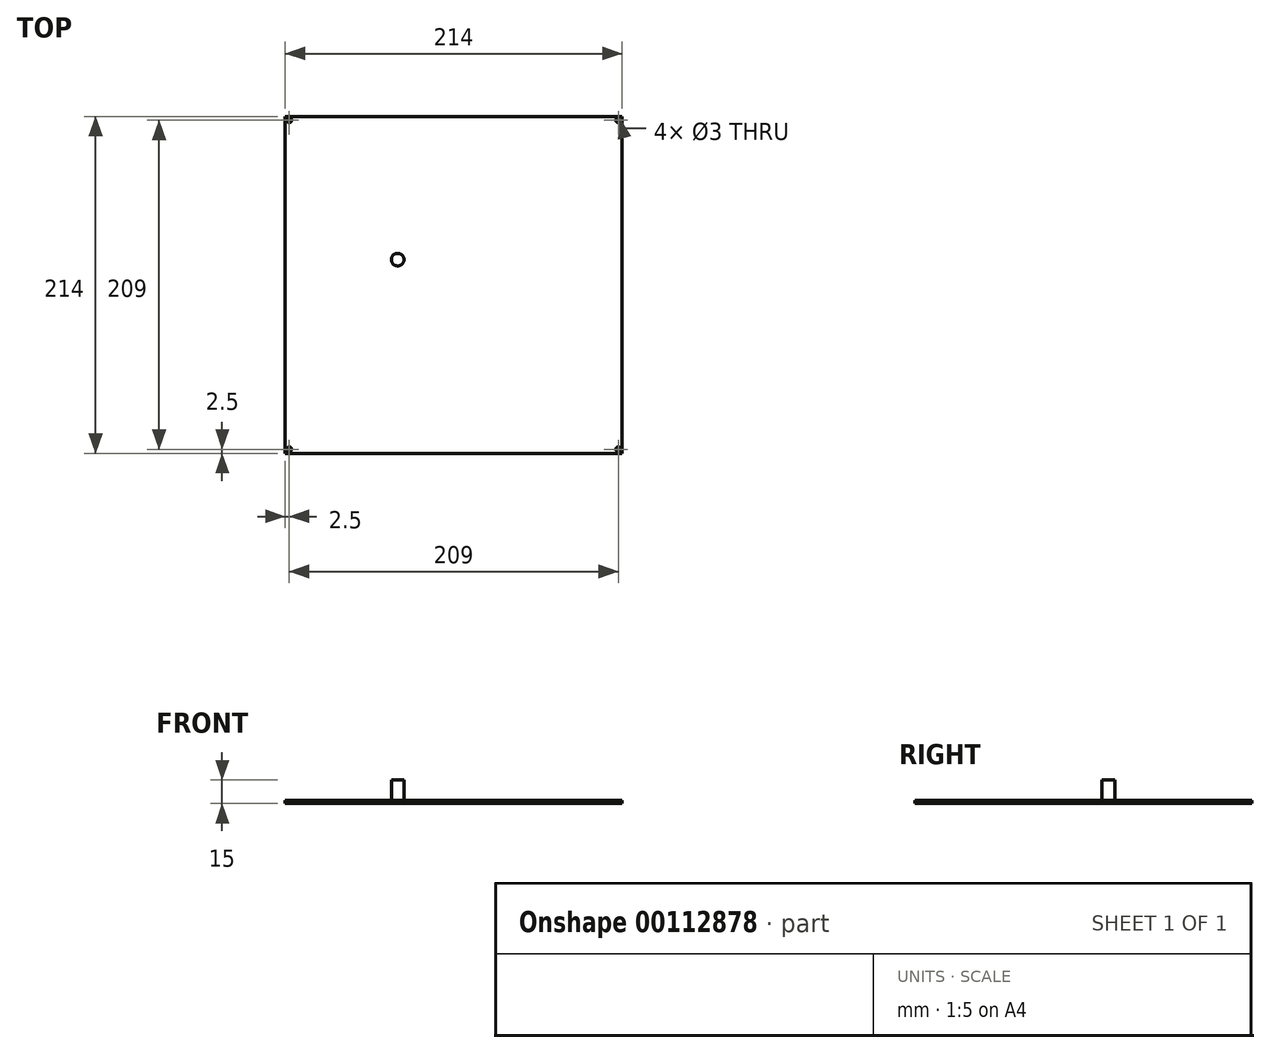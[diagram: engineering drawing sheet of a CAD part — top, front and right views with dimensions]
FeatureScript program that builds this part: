
annotation { "Feature Type Name" : "Feature", "Feature Type Description" : "" }
export const myFeature = defineFeature(function(context is Context, id is Id, definition is map)
    precondition{}
    {
        {
            var Q0;
            Q0=qCreatedBy(makeId("Top.planeOp"),FACE);
            var sketch = newSketch(context, id + "F0", { "sketchPlane" : qUnion([Q0])});
            skLineSegment(sketch, "E0.bottom", {"start": v(107, 107) * mm, "end": v(-107, 107) * mm});
            skLineSegment(sketch, "E0.top", {"start": v(107, -107) * mm, "end": v(-107, -107) * mm});
            skLineSegment(sketch, "E0.left", {"start": v(107, 107) * mm, "end": v(107, -107) * mm});
            skLineSegment(sketch, "E0.right", {"start": v(-107, 107) * mm, "end": v(-107, -107) * mm});
            skPoint(sketch, "E0.middle", {"position": v(0, 0) * mm});
            skLineSegment(sketch, "E1.bottom", {"start": v(104.5, 104.5) * mm, "end": v(-104.5, 104.5) * mm, "construction": true});
            skLineSegment(sketch, "E1.top", {"start": v(104.5, -104.5) * mm, "end": v(-104.5, -104.5) * mm, "construction": true});
            skLineSegment(sketch, "E1.left", {"start": v(104.5, 104.5) * mm, "end": v(104.5, -104.5) * mm, "construction": true});
            skLineSegment(sketch, "E1.right", {"start": v(-104.5, 104.5) * mm, "end": v(-104.5, -104.5) * mm, "construction": true});
            skSolve(sketch);
        }
        {
            var Q0;
            Q0=makeQuery(id+"F0.imprint","IMPRINT",FACE,{"disambiguationData":[TD([[makeQuery(id+"F0.imprint","IMPRINT",EDGE,{"derivedFrom":sQuery(id+"F0.wireOp",EDGE,"E0.bottom")}),1.0]])]});
            extrude(context, id + "F1", {"entities" : qUnion([Q0]), "depth" : 2 * mm});
        }
        {
            var Q0;
            Q0=sQuery(id+"F0.wireOp",VERTEX,"E1.right.start");
            var Q1;
            Q1=sQuery(id+"F0.wireOp",VERTEX,"E1.left.start");
            var Q2;
            Q2=sQuery(id+"F0.wireOp",VERTEX,"E1.right.end");
            var Q3;
            Q3=sQuery(id+"F0.wireOp",VERTEX,"E1.left.end");
            var Q4;
            Q4=makeQuery(id+"F1.opExtrude","SWEPT_BODY",BODY,{"disambiguationData":[OSD([sQuery(id+"F0.wireOp",EDGE,"E0.bottom"),sQuery(id+"F0.wireOp",EDGE,"E0.top"),sQuery(id+"F0.wireOp",EDGE,"E0.left"),sQuery(id+"F0.wireOp",EDGE,"E0.right")])]});
            hole(context, id + "F2", {"style" : HoleStyle.SIMPLE, "endStyle" : HoleEndStyle.THROUGH, "oppositeDirection" : true, "holeDiameter" : 3 * mm, "startFromSketch" : true, "locations" : qUnion([Q0, Q1, Q2, Q3]), "scope" : qUnion([Q4]), "isTappedThrough" : true});
        }
        {
            var Q0;
            Q0=qCreatedBy(makeId("Top.planeOp"),FACE);
            var sketch = newSketch(context, id + "F3", { "sketchPlane" : qUnion([Q0])});
            skCircle(sketch, "E2", {"center": v(-35.61, 16) * mm, "radius": 4 * mm});
            skSolve(sketch);
        }
        {
            var Q0;
            Q0=makeQuery(id+"F3.imprint","IMPRINT",FACE,{"disambiguationData":[TD([[makeQuery(id+"F3.imprint","IMPRINT",EDGE,{"derivedFrom":sQuery(id+"F3.wireOp",EDGE,"E2")}),1.0]])]});
            extrude(context, id + "F4", {"entities" : qUnion([Q0]), "depth" : 15 * mm});
        }
    });
